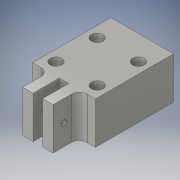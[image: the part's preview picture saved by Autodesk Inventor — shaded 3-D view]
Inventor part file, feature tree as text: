
AUTODESK INVENTOR PART (.ipt)
format: ipt  version: 2016 (Build 200138000, 138)  size: 157,696 bytes
history: native  units: in
note: dims shown in document units (in); Inventor stores cm internally (conversion verified against a paired STEP export)
features: hole x3, extrude x2, sketch x2, pattern_linear x1, fillet x1
ambient origin geometry x8: Origin, YZ Plane, XZ Plane, XY Plane, X Axis, Y Axis, Z Axis, Center Point
bodies: Solid1 (feature_tree)
feature tree (9):
  extrude  "Block"  Depth=3.7283in
  extrude  "Tabs"  Depth=0.5in
  hole  "Arm Mounting Hole"  [1 undecoded]
  hole  "Mounting Hole"  [1 undecoded]
  pattern_linear  "Mounting Holes"  Spacing1=1.25in  [1 undecoded]
  hole  "Spring Hole"  [1 undecoded]
  fillet  "Fillet1"  Radius=0.7874in
  sketch  "Sketch1"  dims[d0=3.0in d1=3.7283in]
  sketch  "Sketch2"  dims[d2=2.0in d3=0.0in d4=0.5in d5=0.45in d6=1.0in d7=0.0in d8=0.5in d9=1.0in d10=0.257in d11=0.75in d12=0.375in d13=0.25in d14=0.5635in d15=1.0in d16=0.8108in d17=1.25in d32=0.598in d39=0.516in d23=0.315in d24=0.75in d25=0.5512in d26=1.2in d27=0.5635in d28=1.0in d29=0.8108in d30=0.7874in d34=1.9685in d35=0.7874in d37=1.9685in d38=1.0in d40=1.378in d41=0.163in d42=0.394in d43=0.375in d44=0.25in d45=0.5635in d46=0.5in d47=0.8108in d48=0.375in]
note: 4 required parameter values undecoded (feature->parameter linkage not recoverable at this tier; creation-order binding heuristic only, values carry confidence <= 0.55)
